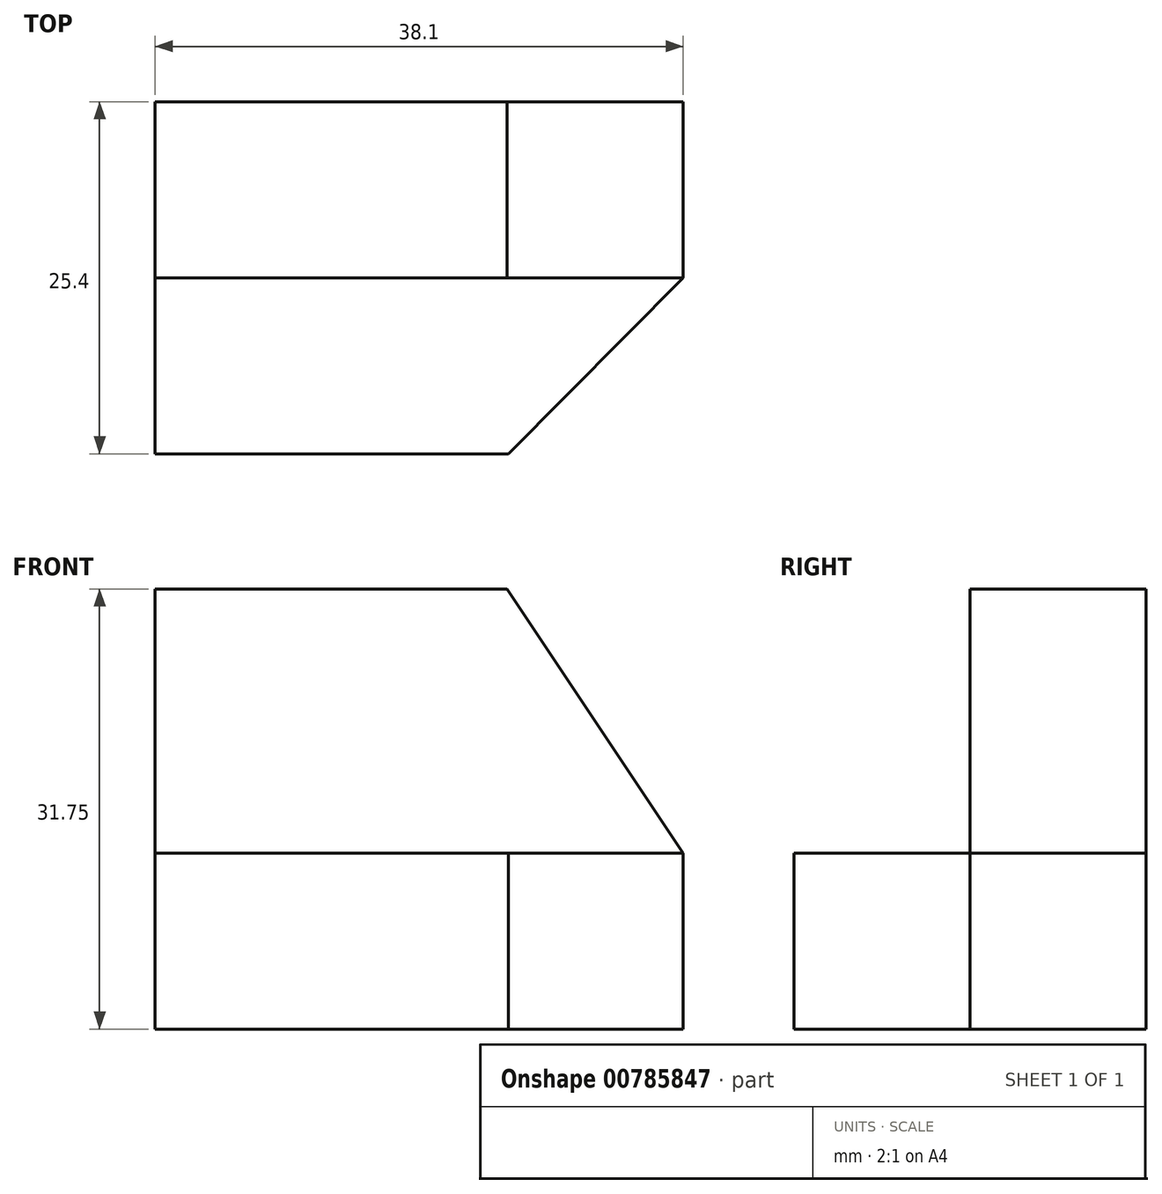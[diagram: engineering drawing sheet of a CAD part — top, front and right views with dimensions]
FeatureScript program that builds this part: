
annotation { "Feature Type Name" : "Feature", "Feature Type Description" : "" }
export const myFeature = defineFeature(function(context is Context, id is Id, definition is map)
    precondition{}
    {
        {
            var Q0;
            Q0=qCreatedBy(makeId("Front.planeOp"),FACE);
            var sketch = newSketch(context, id + "F0", { "sketchPlane" : qUnion([Q0])});
            skLineSegment(sketch, "E0", {"start": v(0, 0) * mm, "end": v(38.1, 0) * mm});
            skLineSegment(sketch, "E1", {"start": v(38.1, 0) * mm, "end": v(38.1, 31.75) * mm});
            skLineSegment(sketch, "E2", {"start": v(38.1, 31.75) * mm, "end": v(0, 31.75) * mm});
            skLineSegment(sketch, "E3", {"start": v(0, 31.75) * mm, "end": v(0, 0) * mm});
            skSolve(sketch);
        }
        {
            var Q0;
            Q0 = qSketchRegion(id + "F0", true);
            extrude(context, id + "F1", {"entities" : qUnion([Q0]), "depth" : 25.4 * mm, "offsetDistance" : 25.4 * mm});
        }
        {
            var Q0;
            Q0=makeQuery(id+"F1.opExtrude","SWEPT_FACE",FACE,{"disambiguationData":[OSD([sQuery(id+"F0.wireOp",EDGE,"E2")])]});
            var sketch = newSketch(context, id + "F2", { "sketchPlane" : qUnion([Q0])});
            skLineSegment(sketch, "E4", {"start": v(0, 0) * mm, "end": v(0, -12.7) * mm});
            skLineSegment(sketch, "E5", {"start": v(0, -12.7) * mm, "end": v(38.1, -12.7) * mm});
            skLineSegment(sketch, "E6", {"start": v(38.1, -12.7) * mm, "end": v(38.1, 0) * mm});
            skLineSegment(sketch, "E7", {"start": v(38.1, 0) * mm, "end": v(0, 0) * mm});
            skLineSegment(sketch, "E8", {"start": v(38.1, -25.4) * mm, "end": v(0, -25.4) * mm});
            skLineSegment(sketch, "E9", {"start": v(0, -25.4) * mm, "end": v(0, -12.7) * mm});
            skLineSegment(sketch, "E10", {"start": v(38.1, -12.7) * mm, "end": v(38.1, -25.4) * mm});
            skSolve(sketch);
        }
        {
            var Q0;
            Q0=makeQuery(id+"F2.imprint","IMPRINT",FACE,{"disambiguationData":[TD([[makeQuery(id+"F2.imprint","IMPRINT",EDGE,{"derivedFrom":sQuery(id+"F2.wireOp",EDGE,"E5")}),-1.0]])]});
            extrude(context, id + "F3", {"entities" : qUnion([Q0]), "operationType" : NewBodyOperationType.REMOVE, "oppositeDirection" : true, "depth" : 19.05 * mm, "offsetDistance" : 25.4 * mm});
        }
        {
            var Q0;
            Q0=makeQuery(id+"F3.boolean.opBoolean","COPY",FACE,{"derivedFrom":makeQuery(id+"F3.opExtrude","CAP_FACE",FACE,{"disambiguationData":[OSD([sQuery(id+"F2.wireOp",EDGE,"E5"),sQuery(id+"F2.wireOp",EDGE,"E8"),sQuery(id+"F2.wireOp",EDGE,"E9"),sQuery(id+"F2.wireOp",EDGE,"E10")])],"isStart":false})});
            var sketch = newSketch(context, id + "F4", { "sketchPlane" : qUnion([Q0])});
            skLineSegment(sketch, "E11", {"start": v(25.5, -25.4) * mm, "end": v(38.1, -12.7) * mm});
            skLineSegment(sketch, "E12", {"start": v(38.1, -12.7) * mm, "end": v(38.1, -25.4) * mm});
            skLineSegment(sketch, "E13", {"start": v(38.1, -25.4) * mm, "end": v(25.5, -25.4) * mm});
            skSolve(sketch);
        }
        {
            var Q0;
            Q0=makeQuery(id+"F4.imprint","IMPRINT",FACE,{"disambiguationData":[TD([[makeQuery(id+"F4.imprint","IMPRINT",EDGE,{"derivedFrom":sQuery(id+"F4.wireOp",EDGE,"E11")}),-1.0]])]});
            extrude(context, id + "F5", {"entities" : qUnion([Q0]), "operationType" : NewBodyOperationType.REMOVE, "oppositeDirection" : true, "depth" : 12.7 * mm, "offsetDistance" : 25.4 * mm});
        }
        {
            var Q0;
            Q0=makeQuery(id+"F3.boolean.opBoolean","COPY",FACE,{"derivedFrom":makeQuery(id+"F3.opExtrude","SWEPT_FACE",FACE,{"disambiguationData":[OSD([sQuery(id+"F2.wireOp",EDGE,"E5")])]})});
            var sketch = newSketch(context, id + "F6", { "sketchPlane" : qUnion([Q0])});
            skLineSegment(sketch, "E14", {"start": v(0, 31.75) * mm, "end": v(25.4, 31.75) * mm});
            skLineSegment(sketch, "E15", {"start": v(25.4, 31.75) * mm, "end": v(38.1, 12.7) * mm});
            skLineSegment(sketch, "E16", {"start": v(38.1, 12.7) * mm, "end": v(38.1, 31.75) * mm});
            skLineSegment(sketch, "E17", {"start": v(38.1, 31.75) * mm, "end": v(25.4, 31.75) * mm});
            skSolve(sketch);
        }
        {
            var Q0;
            Q0=makeQuery(id+"F6.imprint","IMPRINT",FACE,{"disambiguationData":[TD([[makeQuery(id+"F6.imprint","IMPRINT",EDGE,{"derivedFrom":sQuery(id+"F6.wireOp",EDGE,"E15")}),1.0]])]});
            extrude(context, id + "F7", {"entities" : qUnion([Q0]), "operationType" : NewBodyOperationType.REMOVE, "oppositeDirection" : true, "depth" : 12.7 * mm, "offsetDistance" : 25.4 * mm});
        }
    });
